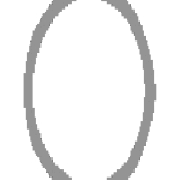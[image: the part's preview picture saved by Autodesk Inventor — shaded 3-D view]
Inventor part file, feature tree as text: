
AUTODESK INVENTOR PART (.ipt)
format: ipt  version: 2021 (Build 250183000, 183)  size: 116,224 bytes
history: native  units: in
note: dims shown in document units (in); Inventor stores cm internally (conversion verified against a paired STEP export)
features: other x4, sketch x3, plane x1
ambient origin geometry x8: Origin, YZ Plane, XZ Plane, XY Plane, X Axis, Y Axis, Z Axis, Center Point
bodies: Solid1 (feature_tree), Body (feature_tree)
feature tree (8):
  other  "Driven Length"
  other  "Frame Generator"
  other  "Start Plane"
  other  "End Plane"
  sketch  "Sketch"  dims[d2=3.5in d4=-0.0in d5=3.5in d6=0.12in d7=0.0in d8=90.0deg d9=3.5in]
  sketch  "Sketch2"  dims[d0=1.0in]
  plane  "Work Plane3"
  sketch  "Sketch3"  dims[d1=0.065in]
